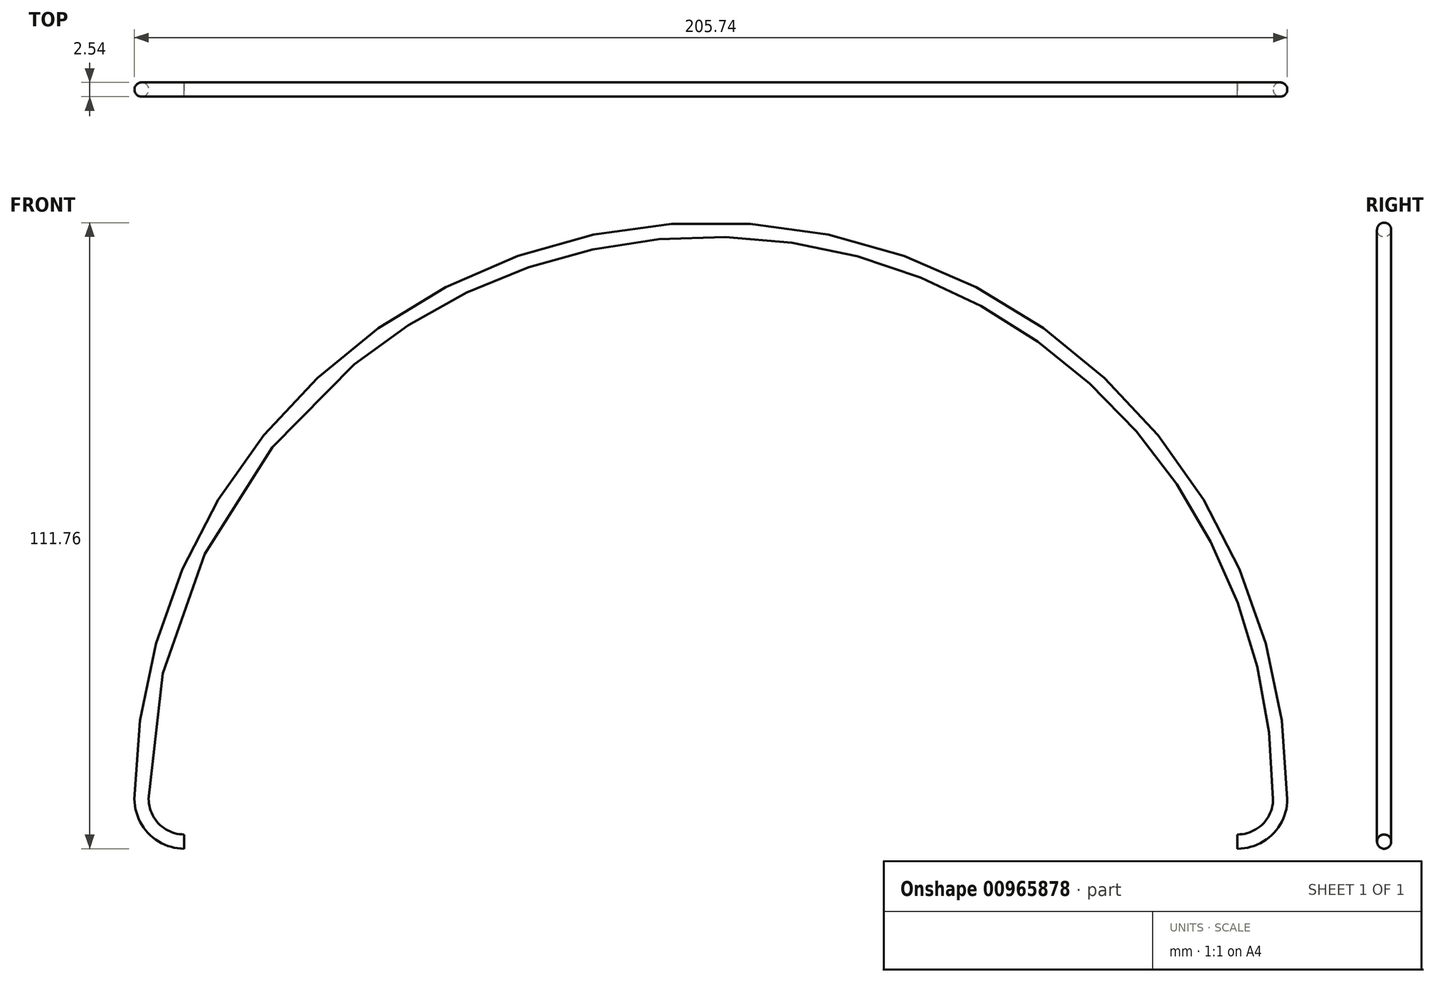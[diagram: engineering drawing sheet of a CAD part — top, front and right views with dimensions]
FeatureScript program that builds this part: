
annotation { "Feature Type Name" : "Feature", "Feature Type Description" : "" }
export const myFeature = defineFeature(function(context is Context, id is Id, definition is map)
    precondition{}
    {
        {
            var Q0;
            Q0=qCreatedBy(makeId("Top.planeOp"),FACE);
            var sketch = newSketch(context, id + "F0", { "sketchPlane" : qUnion([Q0])});
            skLineSegment(sketch, "E0", {"start": v(0, 0) * mm, "end": v(101.6, 0) * mm});
            skLineSegment(sketch, "E1", {"start": v(101.6, 0) * mm, "end": v(-101.6, 0) * mm});
            skCircle(sketch, "E2", {"center": v(-101.6, 0) * mm, "radius": 1.27 * mm});
            skLineSegment(sketch, "E3", {"start": v(0, 0) * mm, "end": v(0, 17.05) * mm});
            skSolve(sketch);
        }
        {
            var Q0;
            Q0=makeQuery(id+"F0.imprint","IMPRINT",FACE,{"disambiguationData":[TD([[makeQuery(id+"F0.imprint","IMPRINT",EDGE,{"derivedFrom":sQuery(id+"F0.wireOp",EDGE,"E2")}),1.0]])]});
            var Q1;
            Q1=sQuery(id+"F0.wireOp",EDGE,"E3");
            revolve(context, id + "F1", {"surfaceOperationType" : NewSurfaceOperationType.NEW, "entities" : qUnion([Q0]), "axis" : qUnion([Q1]), "revolveType" : RevolveType.FULL, "oppositeDirection" : true});
        }
        {
            var Q0;
            Q0=qCreatedBy(makeId("Front.planeOp"),FACE);
            var sketch = newSketch(context, id + "F2", { "sketchPlane" : qUnion([Q0])});
            skLineSegment(sketch, "E4.bottom", {"start": v(-112.6, 0) * mm, "end": v(133.6, 0) * mm});
            skLineSegment(sketch, "E4.top", {"start": v(-112.6, -106.08) * mm, "end": v(133.6, -106.08) * mm});
            skLineSegment(sketch, "E4.left", {"start": v(-112.6, 0) * mm, "end": v(-112.6, -106.08) * mm});
            skLineSegment(sketch, "E4.right", {"start": v(133.6, 0) * mm, "end": v(133.6, -106.08) * mm});
            skSolve(sketch);
        }
        {
            var Q0;
            Q0 = qSketchRegion(id + "F2", true);
            extrude(context, id + "F3", {"entities" : qUnion([Q0]), "operationType" : NewBodyOperationType.REMOVE, "oppositeDirection" : true, "depth" : 25.4 * mm, "offsetDistance" : 25.4 * mm});
        }
        {
            var Q0;
            Q0 = qSketchRegion(id + "F2", true);
            extrude(context, id + "F4", {"entities" : qUnion([Q0]), "operationType" : NewBodyOperationType.REMOVE, "depth" : 51.3 * mm, "offsetDistance" : 25.4 * mm});
        }
        {
            var Q0;
            {var subQ0=sQuery(id+"F2.wireOp",EDGE,"E4.bottom");Q0=makeQuery(id+"F4.boolean.opBoolean","MERGE",FACE,{"derivedFrom":[makeQuery(id+"F3.boolean.opBoolean","COPY",FACE,{"disambiguationData":[OD(1.0)],"derivedFrom":makeQuery(id+"F3.opExtrude","SWEPT_FACE",FACE,{"disambiguationData":[OSD([subQ0])]})})],"fromTools":[makeQuery(id+"F4.opExtrude","SWEPT_FACE",FACE,{"disambiguationData":[OSD([subQ0])]})]});}
            var sketch = newSketch(context, id + "F5", { "sketchPlane" : qUnion([Q0])});
            skCircle(sketch, "E5", {"center": v(101.6, 0) * mm, "radius": 1.27 * mm});
            skLineSegment(sketch, "E6", {"start": v(101.6, 0) * mm, "end": v(93.98, 0) * mm});
            skLineSegment(sketch, "E7", {"start": v(93.98, 0) * mm, "end": v(93.98, 1.42) * mm});
            skSolve(sketch);
        }
        {
            var Q0;
            Q0 = qSketchRegion(id + "F5", true);
            var Q1;
            Q1=sQuery(id+"F5.wireOp",EDGE,"E7");
            revolve(context, id + "F6", {"operationType" : NewBodyOperationType.ADD, "surfaceOperationType" : NewSurfaceOperationType.NEW, "entities" : qUnion([Q0]), "axis" : qUnion([Q1]), "revolveType" : RevolveType.ONE_DIRECTION, "oppositeDirection" : true, "angle" : 90 * degree});
        }
        {
            var Q0;
            {var subQ0=sQuery(id+"F2.wireOp",EDGE,"E4.bottom");Q0=makeQuery(id+"F4.boolean.opBoolean","MERGE",FACE,{"derivedFrom":[makeQuery(id+"F3.boolean.opBoolean","COPY",FACE,{"disambiguationData":[OD(0.0)],"derivedFrom":makeQuery(id+"F3.opExtrude","SWEPT_FACE",FACE,{"disambiguationData":[OSD([subQ0])]})})],"fromTools":[makeQuery(id+"F4.opExtrude","SWEPT_FACE",FACE,{"disambiguationData":[OSD([subQ0])]})]});}
            var sketch = newSketch(context, id + "F7", { "sketchPlane" : qUnion([Q0])});
            skCircle(sketch, "E8", {"center": v(-101.6, 0) * mm, "radius": 1.27 * mm});
            skLineSegment(sketch, "E9", {"start": v(-101.6, 0) * mm, "end": v(-93.98, 0) * mm});
            skLineSegment(sketch, "E10", {"start": v(-93.98, 0) * mm, "end": v(-93.98, 2.04) * mm});
            skSolve(sketch);
        }
        {
            var Q0;
            Q0 = qSketchRegion(id + "F7", true);
            var Q1;
            Q1=sQuery(id+"F7.wireOp",EDGE,"E10");
            revolve(context, id + "F8", {"operationType" : NewBodyOperationType.ADD, "surfaceOperationType" : NewSurfaceOperationType.NEW, "entities" : qUnion([Q0]), "axis" : qUnion([Q1]), "revolveType" : RevolveType.ONE_DIRECTION, "angle" : 90 * degree});
        }
    });
